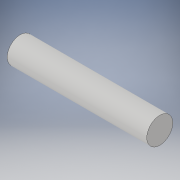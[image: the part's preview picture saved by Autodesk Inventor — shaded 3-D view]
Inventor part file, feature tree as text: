
AUTODESK INVENTOR PART (.ipt)
format: ipt  version: 2017 (Build 210142000, 142)  size: 88,576 bytes
history: native  units: in
note: dims shown in document units (in); Inventor stores cm internally (conversion verified against a paired STEP export)
features: extrude x1, sketch x1
ambient origin geometry x8: Origin, YZ Plane, XZ Plane, XY Plane, X Axis, Y Axis, Z Axis, Center Point
bodies: Solid1 (feature_tree)
feature tree (2):
  extrude  "Extrusion1"  Depth=1.34in TaperAngle=0.0deg
  sketch  "Sketch1"  dims[d0=0.25in d1=1.34in d2=0.0in]
